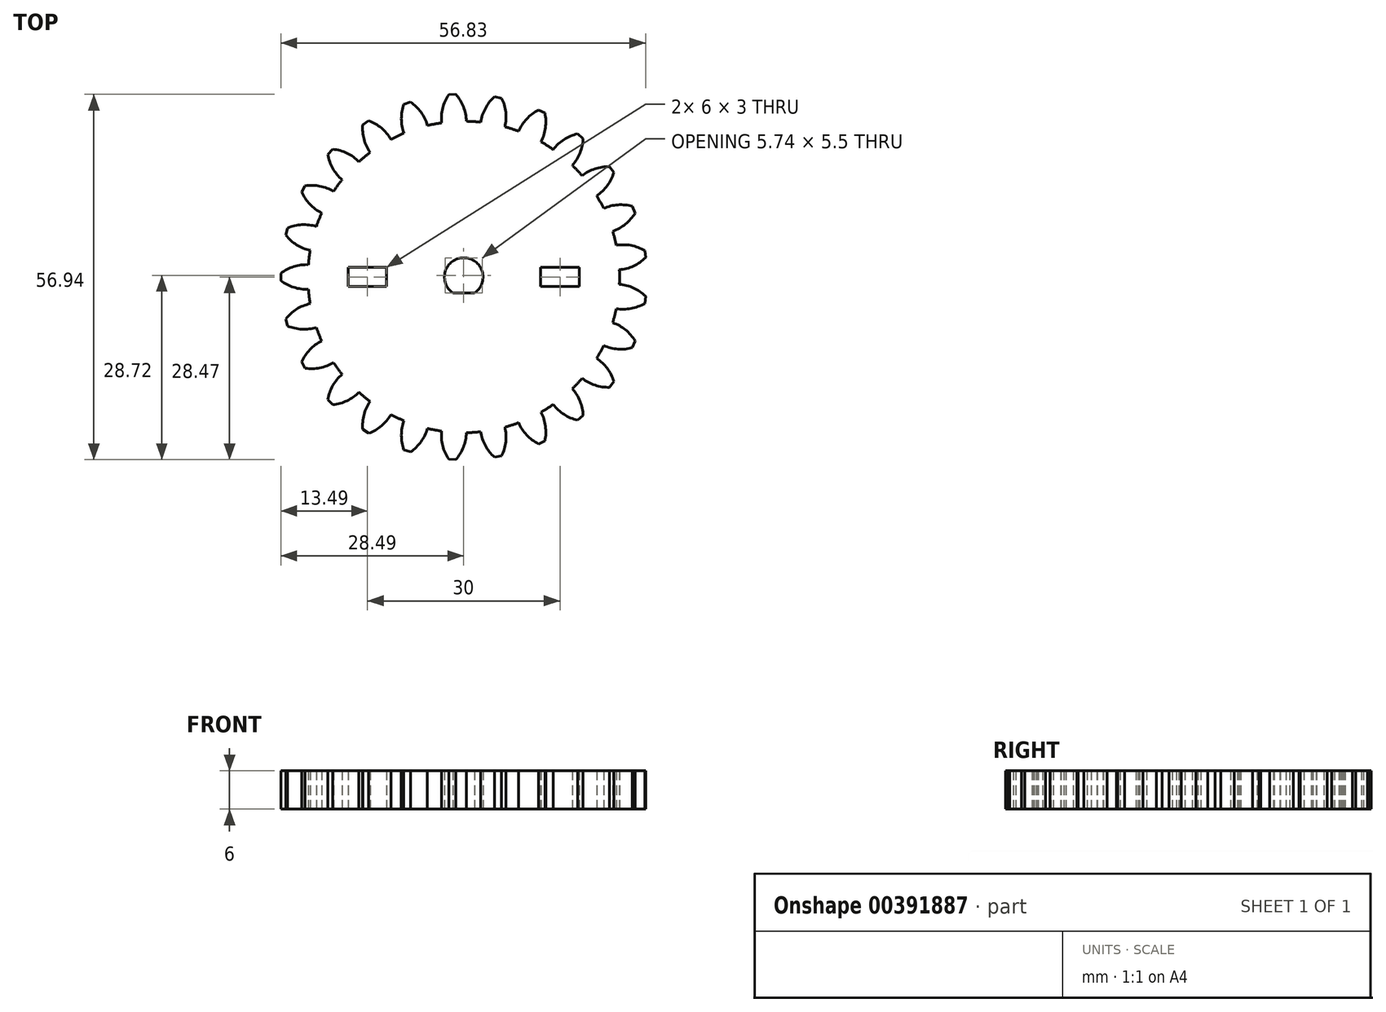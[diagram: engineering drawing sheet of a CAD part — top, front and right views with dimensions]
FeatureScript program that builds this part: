
annotation { "Feature Type Name" : "Feature", "Feature Type Description" : "" }
export const myFeature = defineFeature(function(context is Context, id is Id, definition is map)
    precondition{}
    {
        {
            assignVariable(context, id + "F0", {"name" : "GearDepth", "anyValue" : 6});
        }
        {
            var Q0;
            Q0=qCreatedBy(makeId("Top.planeOp"),FACE);
            var sketch = newSketch(context, id + "F1", { "sketchPlane" : qUnion([Q0])});
            skCircle(sketch, "E0", {"center": v(0, 0) * mm, "radius": 24.28 * mm, "construction": true});
            skCircle(sketch, "E1", {"center": v(0, 0) * mm, "radius": 26.39 * mm, "construction": true});
            skCircle(sketch, "E2", {"center": v(0, 0) * mm, "radius": 28.5 * mm, "construction": true});
            skLineSegment(sketch, "E3", {"start": v(0, 0) * mm, "end": v(0, 17.6) * mm, "construction": true});
            skLineSegment(sketch, "E4", {"start": v(0, 0) * mm, "end": v(-1.13, 18.01) * mm, "construction": true});
            skLineSegment(sketch, "E5", {"start": v(0, 26.39) * mm, "end": v(-10.54, 26.39) * mm, "construction": true});
            skLineSegment(sketch, "E6", {"start": v(0, 26.39) * mm, "end": v(-15.41, 20.78) * mm, "construction": true});
            skCircle(sketch, "E7", {"center": v(0, 26.39) * mm, "radius": 6.6 * mm, "construction": true});
            skCircle(sketch, "E8", {"center": v(-6.2, 24.13) * mm, "radius": 6.6 * mm, "construction": true});
            skArc(sketch, "E9.trimOffspring", {"start": v(0.4, 24.27) * mm, "mid": v(-0.05, 26.52) * mm, "end": v(-1.23, 28.47) * mm});
            skArc(sketch, "E10.MirrorCS", {"start": v(-3.44, 24.03) * mm, "mid": v(-3.28, 26.31) * mm, "end": v(-2.35, 28.4) * mm});
            skLineSegment(sketch, "E11", {"start": v(-2.35, 28.4) * mm, "end": v(-1.23, 28.47) * mm});
            skArc(sketch, "E12.1.0", {"start": v(-9.3, 22.42) * mm, "mid": v(-9.72, 24.67) * mm, "end": v(-9.34, 26.93) * mm});
            skArc(sketch, "E12.1.1", {"start": v(-5.65, 23.61) * mm, "mid": v(-6.64, 25.67) * mm, "end": v(-8.27, 27.27) * mm});
            skLineSegment(sketch, "E12.1.2", {"start": v(-9.34, 26.93) * mm, "end": v(-8.27, 27.27) * mm});
            skArc(sketch, "E12.2.0", {"start": v(-14.59, 19.4) * mm, "mid": v(-15.55, 21.48) * mm, "end": v(-15.74, 23.76) * mm});
            skArc(sketch, "E12.2.1", {"start": v(-11.35, 21.46) * mm, "mid": v(-12.82, 23.21) * mm, "end": v(-14.8, 24.36) * mm});
            skLineSegment(sketch, "E12.2.2", {"start": v(-15.74, 23.76) * mm, "end": v(-14.8, 24.36) * mm});
            skArc(sketch, "E12.3.0", {"start": v(-18.96, 15.17) * mm, "mid": v(-20.4, 16.94) * mm, "end": v(-21.15, 19.1) * mm});
            skArc(sketch, "E12.3.1", {"start": v(-16.33, 17.97) * mm, "mid": v(-18.19, 19.3) * mm, "end": v(-20.39, 19.91) * mm});
            skLineSegment(sketch, "E12.3.2", {"start": v(-21.15, 19.1) * mm, "end": v(-20.39, 19.91) * mm});
            skArc(sketch, "E12.4.0", {"start": v(-22.13, 9.98) * mm, "mid": v(-23.97, 11.33) * mm, "end": v(-25.24, 13.24) * mm});
            skArc(sketch, "E12.4.1", {"start": v(-20.28, 13.34) * mm, "mid": v(-22.42, 14.17) * mm, "end": v(-24.7, 14.22) * mm});
            skLineSegment(sketch, "E12.4.2", {"start": v(-25.24, 13.24) * mm, "end": v(-24.7, 14.22) * mm});
            skArc(sketch, "E12.5.0", {"start": v(-23.92, 4.16) * mm, "mid": v(-26.04, 5.02) * mm, "end": v(-27.74, 6.55) * mm});
            skArc(sketch, "E12.5.1", {"start": v(-22.96, 7.88) * mm, "mid": v(-25.23, 8.15) * mm, "end": v(-27.46, 7.63) * mm});
            skLineSegment(sketch, "E12.5.2", {"start": v(-27.74, 6.55) * mm, "end": v(-27.46, 7.63) * mm});
            skArc(sketch, "E12.6.0", {"start": v(-24.2, -1.92) * mm, "mid": v(-26.47, -1.62) * mm, "end": v(-28.5, -0.56) * mm});
            skArc(sketch, "E12.6.1", {"start": v(-24.2, 1.92) * mm, "mid": v(-26.47, 1.62) * mm, "end": v(-28.5, 0.56) * mm});
            skLineSegment(sketch, "E12.6.2", {"start": v(-28.5, -0.56) * mm, "end": v(-28.5, 0.56) * mm});
            skArc(sketch, "E12.7.0", {"start": v(-22.96, -7.88) * mm, "mid": v(-25.23, -8.15) * mm, "end": v(-27.46, -7.63) * mm});
            skArc(sketch, "E12.7.1", {"start": v(-23.92, -4.16) * mm, "mid": v(-26.04, -5.02) * mm, "end": v(-27.74, -6.55) * mm});
            skLineSegment(sketch, "E12.7.2", {"start": v(-27.46, -7.63) * mm, "end": v(-27.74, -6.55) * mm});
            skArc(sketch, "E12.8.0", {"start": v(-20.28, -13.34) * mm, "mid": v(-22.42, -14.17) * mm, "end": v(-24.7, -14.22) * mm});
            skArc(sketch, "E12.8.1", {"start": v(-22.13, -9.98) * mm, "mid": v(-23.97, -11.33) * mm, "end": v(-25.24, -13.24) * mm});
            skLineSegment(sketch, "E12.8.2", {"start": v(-24.7, -14.22) * mm, "end": v(-25.24, -13.24) * mm});
            skArc(sketch, "E12.9.0", {"start": v(-16.33, -17.97) * mm, "mid": v(-18.19, -19.3) * mm, "end": v(-20.39, -19.91) * mm});
            skArc(sketch, "E12.9.1", {"start": v(-18.96, -15.17) * mm, "mid": v(-20.4, -16.94) * mm, "end": v(-21.15, -19.1) * mm});
            skLineSegment(sketch, "E12.9.2", {"start": v(-20.39, -19.91) * mm, "end": v(-21.15, -19.1) * mm});
            skArc(sketch, "E13", {"start": v(-3.44, 24.03) * mm, "mid": v(-4.55, 23.85) * mm, "end": v(-5.65, 23.61) * mm});
            skArc(sketch, "E14.1.0", {"start": v(-9.3, 22.42) * mm, "mid": v(-10.34, 21.97) * mm, "end": v(-11.35, 21.46) * mm});
            skArc(sketch, "E14.2.0", {"start": v(-14.59, 19.4) * mm, "mid": v(-15.48, 18.7) * mm, "end": v(-16.33, 17.97) * mm});
            skArc(sketch, "E14.3.0", {"start": v(-18.96, 15.17) * mm, "mid": v(-19.64, 14.27) * mm, "end": v(-20.28, 13.34) * mm});
            skArc(sketch, "E14.4.0", {"start": v(-22.13, 9.98) * mm, "mid": v(-22.57, 8.94) * mm, "end": v(-22.96, 7.88) * mm});
            skArc(sketch, "E14.5.0", {"start": v(-23.92, 4.16) * mm, "mid": v(-24.09, 3.04) * mm, "end": v(-24.2, 1.92) * mm});
            skArc(sketch, "E14.6.0", {"start": v(-24.2, -1.92) * mm, "mid": v(-24.09, -3.04) * mm, "end": v(-23.92, -4.16) * mm});
            skArc(sketch, "E14.7.0", {"start": v(-22.96, -7.88) * mm, "mid": v(-22.57, -8.94) * mm, "end": v(-22.13, -9.98) * mm});
            skArc(sketch, "E14.8.0", {"start": v(-20.28, -13.34) * mm, "mid": v(-19.64, -14.27) * mm, "end": v(-18.96, -15.17) * mm});
            skArc(sketch, "E14.9.0", {"start": v(-16.33, -17.97) * mm, "mid": v(-15.48, -18.7) * mm, "end": v(-14.59, -19.4) * mm});
            skArc(sketch, "E15.3.10.0", {"start": v(-11.35, -21.46) * mm, "mid": v(-10.34, -21.97) * mm, "end": v(-9.3, -22.42) * mm});
            skArc(sketch, "E15.3.11.0", {"start": v(-5.65, -23.61) * mm, "mid": v(-4.55, -23.85) * mm, "end": v(-3.44, -24.03) * mm});
            skArc(sketch, "E15.3.12.0", {"start": v(0.4, -24.27) * mm, "mid": v(1.52, -24.23) * mm, "end": v(2.65, -24.13) * mm});
            skArc(sketch, "E15.3.13.0", {"start": v(6.42, -23.41) * mm, "mid": v(7.5, -23.09) * mm, "end": v(8.57, -22.72) * mm});
            skArc(sketch, "E15.3.14.0", {"start": v(12.04, -21.08) * mm, "mid": v(13, -20.5) * mm, "end": v(13.95, -19.87) * mm});
            skArc(sketch, "E16.4.10.0", {"start": v(-14.59, -19.4) * mm, "mid": v(-15.55, -21.48) * mm, "end": v(-15.74, -23.76) * mm});
            skArc(sketch, "E16.5.10.0", {"start": v(-11.35, -21.46) * mm, "mid": v(-12.82, -23.21) * mm, "end": v(-14.8, -24.36) * mm});
            skLineSegment(sketch, "E16.8.10.0", {"start": v(-14.8, -24.36) * mm, "end": v(-15.74, -23.76) * mm});
            skArc(sketch, "E16.4.11.0", {"start": v(-9.3, -22.42) * mm, "mid": v(-9.72, -24.67) * mm, "end": v(-9.34, -26.93) * mm});
            skArc(sketch, "E16.5.11.0", {"start": v(-5.65, -23.61) * mm, "mid": v(-6.64, -25.67) * mm, "end": v(-8.27, -27.27) * mm});
            skLineSegment(sketch, "E16.8.11.0", {"start": v(-8.27, -27.27) * mm, "end": v(-9.34, -26.93) * mm});
            skArc(sketch, "E16.4.12.0", {"start": v(-3.44, -24.03) * mm, "mid": v(-3.28, -26.31) * mm, "end": v(-2.35, -28.4) * mm});
            skArc(sketch, "E16.5.12.0", {"start": v(0.4, -24.27) * mm, "mid": v(-0.05, -26.52) * mm, "end": v(-1.23, -28.47) * mm});
            skLineSegment(sketch, "E16.8.12.0", {"start": v(-1.23, -28.47) * mm, "end": v(-2.35, -28.4) * mm});
            skArc(sketch, "E16.4.13.0", {"start": v(2.65, -24.13) * mm, "mid": v(3.37, -26.3) * mm, "end": v(4.8, -28.1) * mm});
            skArc(sketch, "E16.5.13.0", {"start": v(6.42, -23.41) * mm, "mid": v(6.55, -25.7) * mm, "end": v(5.89, -27.89) * mm});
            skLineSegment(sketch, "E16.8.13.0", {"start": v(5.89, -27.89) * mm, "end": v(4.8, -28.1) * mm});
            skArc(sketch, "E16.4.14.0", {"start": v(8.57, -22.72) * mm, "mid": v(9.8, -24.64) * mm, "end": v(11.63, -26.02) * mm});
            skArc(sketch, "E16.5.14.0", {"start": v(12.04, -21.08) * mm, "mid": v(12.73, -23.26) * mm, "end": v(12.64, -25.54) * mm});
            skLineSegment(sketch, "E16.8.14.0", {"start": v(12.64, -25.54) * mm, "end": v(11.63, -26.02) * mm});
            skArc(sketch, "E17.3.15.0", {"start": v(16.9, -17.42) * mm, "mid": v(17.7, -16.62) * mm, "end": v(18.45, -15.78) * mm});
            skArc(sketch, "E17.3.16.0", {"start": v(20.7, -12.67) * mm, "mid": v(21.27, -11.7) * mm, "end": v(21.8, -10.7) * mm});
            skArc(sketch, "E17.3.17.0", {"start": v(23.2, -7.12) * mm, "mid": v(23.52, -6.04) * mm, "end": v(23.77, -4.94) * mm});
            skArc(sketch, "E17.3.18.0", {"start": v(24.25, -1.13) * mm, "mid": v(24.28, 0) * mm, "end": v(24.25, 1.13) * mm});
            skArc(sketch, "E17.3.19.0", {"start": v(23.77, 4.94) * mm, "mid": v(23.52, 6.04) * mm, "end": v(23.2, 7.12) * mm});
            skArc(sketch, "E18.4.15.0", {"start": v(13.95, -19.87) * mm, "mid": v(15.63, -21.42) * mm, "end": v(17.73, -22.31) * mm});
            skArc(sketch, "E18.5.15.0", {"start": v(16.9, -17.42) * mm, "mid": v(18.12, -19.36) * mm, "end": v(18.6, -21.6) * mm});
            skLineSegment(sketch, "E18.8.15.0", {"start": v(18.6, -21.6) * mm, "end": v(17.73, -22.31) * mm});
            skArc(sketch, "E18.4.16.0", {"start": v(18.45, -15.78) * mm, "mid": v(20.46, -16.87) * mm, "end": v(22.72, -17.2) * mm});
            skArc(sketch, "E18.5.16.0", {"start": v(20.7, -12.67) * mm, "mid": v(22.36, -14.25) * mm, "end": v(23.38, -16.3) * mm});
            skLineSegment(sketch, "E18.8.16.0", {"start": v(23.38, -16.3) * mm, "end": v(22.72, -17.2) * mm});
            skArc(sketch, "E18.4.17.0", {"start": v(21.8, -10.7) * mm, "mid": v(24.01, -11.25) * mm, "end": v(26.29, -11) * mm});
            skArc(sketch, "E18.5.17.0", {"start": v(23.2, -7.12) * mm, "mid": v(25.2, -8.24) * mm, "end": v(26.7, -9.97) * mm});
            skLineSegment(sketch, "E18.8.17.0", {"start": v(26.7, -9.97) * mm, "end": v(26.29, -11) * mm});
            skArc(sketch, "E18.4.18.0", {"start": v(23.77, -4.94) * mm, "mid": v(26.06, -4.92) * mm, "end": v(28.2, -4.13) * mm});
            skArc(sketch, "E18.5.18.0", {"start": v(24.25, -1.13) * mm, "mid": v(26.46, -1.71) * mm, "end": v(28.34, -3.02) * mm});
            skLineSegment(sketch, "E18.8.18.0", {"start": v(28.34, -3.02) * mm, "end": v(28.2, -4.13) * mm});
            skArc(sketch, "E18.4.19.0", {"start": v(24.25, 1.13) * mm, "mid": v(26.46, 1.71) * mm, "end": v(28.34, 3.02) * mm});
            skArc(sketch, "E18.5.19.0", {"start": v(23.77, 4.94) * mm, "mid": v(26.06, 4.92) * mm, "end": v(28.2, 4.13) * mm});
            skLineSegment(sketch, "E18.8.19.0", {"start": v(28.2, 4.13) * mm, "end": v(28.34, 3.02) * mm});
            skCircle(sketch, "E19", {"center": v(0, 0) * mm, "radius": 2.5 * mm, "construction": true});
            skArc(sketch, "E20.3.20.0", {"start": v(21.8, 10.7) * mm, "mid": v(21.27, 11.7) * mm, "end": v(20.7, 12.67) * mm});
            skArc(sketch, "E20.3.21.0", {"start": v(18.45, 15.78) * mm, "mid": v(17.7, 16.62) * mm, "end": v(16.9, 17.42) * mm});
            skArc(sketch, "E20.3.22.0", {"start": v(13.95, 19.87) * mm, "mid": v(13, 20.5) * mm, "end": v(12.04, 21.08) * mm});
            skArc(sketch, "E20.3.23.0", {"start": v(8.57, 22.72) * mm, "mid": v(7.5, 23.09) * mm, "end": v(6.42, 23.41) * mm});
            skArc(sketch, "E20.3.24.0", {"start": v(2.65, 24.13) * mm, "mid": v(1.52, 24.23) * mm, "end": v(0.4, 24.27) * mm});
            skArc(sketch, "E21.4.20.0", {"start": v(23.2, 7.12) * mm, "mid": v(25.2, 8.24) * mm, "end": v(26.7, 9.97) * mm});
            skArc(sketch, "E21.5.20.0", {"start": v(21.8, 10.7) * mm, "mid": v(24.01, 11.25) * mm, "end": v(26.29, 11) * mm});
            skLineSegment(sketch, "E21.8.20.0", {"start": v(26.29, 11) * mm, "end": v(26.7, 9.97) * mm});
            skArc(sketch, "E21.4.21.0", {"start": v(20.7, 12.67) * mm, "mid": v(22.36, 14.25) * mm, "end": v(23.38, 16.3) * mm});
            skArc(sketch, "E21.5.21.0", {"start": v(18.45, 15.78) * mm, "mid": v(20.46, 16.87) * mm, "end": v(22.72, 17.2) * mm});
            skLineSegment(sketch, "E21.8.21.0", {"start": v(22.72, 17.2) * mm, "end": v(23.38, 16.3) * mm});
            skArc(sketch, "E21.4.22.0", {"start": v(16.9, 17.42) * mm, "mid": v(18.12, 19.36) * mm, "end": v(18.6, 21.6) * mm});
            skArc(sketch, "E21.5.22.0", {"start": v(13.95, 19.87) * mm, "mid": v(15.63, 21.42) * mm, "end": v(17.73, 22.31) * mm});
            skLineSegment(sketch, "E21.8.22.0", {"start": v(17.73, 22.31) * mm, "end": v(18.6, 21.6) * mm});
            skArc(sketch, "E21.4.23.0", {"start": v(12.04, 21.08) * mm, "mid": v(12.73, 23.26) * mm, "end": v(12.64, 25.54) * mm});
            skArc(sketch, "E21.5.23.0", {"start": v(8.57, 22.72) * mm, "mid": v(9.8, 24.64) * mm, "end": v(11.63, 26.02) * mm});
            skLineSegment(sketch, "E21.8.23.0", {"start": v(11.63, 26.02) * mm, "end": v(12.64, 25.54) * mm});
            skArc(sketch, "E21.4.24.0", {"start": v(6.42, 23.41) * mm, "mid": v(6.55, 25.7) * mm, "end": v(5.89, 27.89) * mm});
            skArc(sketch, "E21.5.24.0", {"start": v(2.65, 24.13) * mm, "mid": v(3.37, 26.3) * mm, "end": v(4.8, 28.1) * mm});
            skLineSegment(sketch, "E21.8.24.0", {"start": v(4.8, 28.1) * mm, "end": v(5.89, 27.89) * mm});
            skLineSegment(sketch, "E22", {"start": v(-1.66, -2.5) * mm, "end": v(1.66, -2.5) * mm});
            skArc(sketch, "E23", {"start": v(-1.66, -2.5) * mm, "mid": v(0, 3) * mm, "end": v(1.66, -2.5) * mm});
            skLineSegment(sketch, "E24.bottom", {"start": v(18, -1.5) * mm, "end": v(12, -1.5) * mm});
            skLineSegment(sketch, "E24.top", {"start": v(18, 1.5) * mm, "end": v(12, 1.5) * mm});
            skLineSegment(sketch, "E24.left", {"start": v(18, -1.5) * mm, "end": v(18, 1.5) * mm});
            skLineSegment(sketch, "E24.right", {"start": v(12, -1.5) * mm, "end": v(12, 1.5) * mm});
            skPoint(sketch, "E24.middle", {"position": v(15, 0) * mm});
            skLineSegment(sketch, "E25.bottom", {"start": v(-12, -1.5) * mm, "end": v(-18, -1.5) * mm});
            skLineSegment(sketch, "E25.top", {"start": v(-12, 1.5) * mm, "end": v(-18, 1.5) * mm});
            skLineSegment(sketch, "E25.left", {"start": v(-12, -1.5) * mm, "end": v(-12, 1.5) * mm});
            skLineSegment(sketch, "E25.right", {"start": v(-18, -1.5) * mm, "end": v(-18, 1.5) * mm});
            skPoint(sketch, "E25.middle", {"position": v(-15, 0) * mm});
            skSolve(sketch);
        }
        {
            var Q0;
            {var subQ0=sQuery(id+"F1.wireOp",EDGE,"E9.trimOffspring");Q0=makeQuery(id+"F1.imprint","IMPRINT",FACE,{"disambiguationData":[TD([[makeQuery(id+"F1.imprint","IMPRINT",EDGE,{"derivedFrom":subQ0}),1.0]])]});}
            var Q1;
            {var subQ0=sQuery(id+"F1.wireOp",EDGE,"E0");var subQ1=makeQuery(id+"F1.imprint","INTERSECT",VERTEX,{"derivedFrom":[subQ0,sQuery(id+"F1.wireOp",EDGE,"E9.trimOffspring")]});Q1=makeQuery(id+"F1.imprint","IMPRINT",FACE,{"disambiguationData":[TD([[makeQuery(id+"F1.imprint","IMPRINT",EDGE,{"disambiguationData":[TD([[subQ1,-1.0]])],"derivedFrom":subQ0}),1.0]])]});}
            var Q2;
            {var subQ0=sQuery(id+"F1.wireOp",EDGE,"ff0f1e59-5a19-46eb-ac47-c6f22bc8a670.1.0");Q2=makeQuery(id+"F1.imprint","IMPRINT",FACE,{"disambiguationData":[TD([[makeQuery(id+"F1.imprint","IMPRINT",EDGE,{"derivedFrom":subQ0}),1.0]])]});}
            var Q3;
            {var subQ0=sQuery(id+"F1.wireOp",EDGE,"ff0f1e59-5a19-46eb-ac47-c6f22bc8a670.2.0");Q3=makeQuery(id+"F1.imprint","IMPRINT",FACE,{"disambiguationData":[TD([[makeQuery(id+"F1.imprint","IMPRINT",EDGE,{"derivedFrom":subQ0}),1.0]])]});}
            var Q4;
            {var subQ0=sQuery(id+"F1.wireOp",EDGE,"ff0f1e59-5a19-46eb-ac47-c6f22bc8a670.3.0");Q4=makeQuery(id+"F1.imprint","IMPRINT",FACE,{"disambiguationData":[TD([[makeQuery(id+"F1.imprint","IMPRINT",EDGE,{"derivedFrom":subQ0}),1.0]])]});}
            var Q5;
            {var subQ0=sQuery(id+"F1.wireOp",EDGE,"ff0f1e59-5a19-46eb-ac47-c6f22bc8a670.4.0");Q5=makeQuery(id+"F1.imprint","IMPRINT",FACE,{"disambiguationData":[TD([[makeQuery(id+"F1.imprint","IMPRINT",EDGE,{"derivedFrom":subQ0}),1.0]])]});}
            var Q6;
            {var subQ0=sQuery(id+"F1.wireOp",EDGE,"ff0f1e59-5a19-46eb-ac47-c6f22bc8a670.5.0");Q6=makeQuery(id+"F1.imprint","IMPRINT",FACE,{"disambiguationData":[TD([[makeQuery(id+"F1.imprint","IMPRINT",EDGE,{"derivedFrom":subQ0}),1.0]])]});}
            var Q7;
            {var subQ0=sQuery(id+"F1.wireOp",EDGE,"ff0f1e59-5a19-46eb-ac47-c6f22bc8a670.6.0");Q7=makeQuery(id+"F1.imprint","IMPRINT",FACE,{"disambiguationData":[TD([[makeQuery(id+"F1.imprint","IMPRINT",EDGE,{"derivedFrom":subQ0}),1.0]])]});}
            var Q8;
            {var subQ0=sQuery(id+"F1.wireOp",EDGE,"ff0f1e59-5a19-46eb-ac47-c6f22bc8a670.7.0");Q8=makeQuery(id+"F1.imprint","IMPRINT",FACE,{"disambiguationData":[TD([[makeQuery(id+"F1.imprint","IMPRINT",EDGE,{"derivedFrom":subQ0}),1.0]])]});}
            var Q9;
            {var subQ0=sQuery(id+"F1.wireOp",EDGE,"ff0f1e59-5a19-46eb-ac47-c6f22bc8a670.8.0");Q9=makeQuery(id+"F1.imprint","IMPRINT",FACE,{"disambiguationData":[TD([[makeQuery(id+"F1.imprint","IMPRINT",EDGE,{"derivedFrom":subQ0}),1.0]])]});}
            var Q10;
            {var subQ0=sQuery(id+"F1.wireOp",EDGE,"ff0f1e59-5a19-46eb-ac47-c6f22bc8a670.9.0");Q10=makeQuery(id+"F1.imprint","IMPRINT",FACE,{"disambiguationData":[TD([[makeQuery(id+"F1.imprint","IMPRINT",EDGE,{"derivedFrom":subQ0}),1.0]])]});}
            var Q11;
            {var subQ0=sQuery(id+"F1.wireOp",EDGE,"ff0f1e59-5a19-46eb-ac47-c6f22bc8a670.10.0");Q11=makeQuery(id+"F1.imprint","IMPRINT",FACE,{"disambiguationData":[TD([[makeQuery(id+"F1.imprint","IMPRINT",EDGE,{"derivedFrom":subQ0}),1.0]])]});}
            var Q12;
            {var subQ0=sQuery(id+"F1.wireOp",EDGE,"ff0f1e59-5a19-46eb-ac47-c6f22bc8a670.11.0");Q12=makeQuery(id+"F1.imprint","IMPRINT",FACE,{"disambiguationData":[TD([[makeQuery(id+"F1.imprint","IMPRINT",EDGE,{"derivedFrom":subQ0}),1.0]])]});}
            var Q13;
            {var subQ0=sQuery(id+"F1.wireOp",EDGE,"ff0f1e59-5a19-46eb-ac47-c6f22bc8a670.12.0");Q13=makeQuery(id+"F1.imprint","IMPRINT",FACE,{"disambiguationData":[TD([[makeQuery(id+"F1.imprint","IMPRINT",EDGE,{"derivedFrom":subQ0}),1.0]])]});}
            var Q14;
            {var subQ0=sQuery(id+"F1.wireOp",EDGE,"ff0f1e59-5a19-46eb-ac47-c6f22bc8a670.13.0");Q14=makeQuery(id+"F1.imprint","IMPRINT",FACE,{"disambiguationData":[TD([[makeQuery(id+"F1.imprint","IMPRINT",EDGE,{"derivedFrom":subQ0}),1.0]])]});}
            var Q15;
            {var subQ0=sQuery(id+"F1.wireOp",EDGE,"ff0f1e59-5a19-46eb-ac47-c6f22bc8a670.14.0");Q15=makeQuery(id+"F1.imprint","IMPRINT",FACE,{"disambiguationData":[TD([[makeQuery(id+"F1.imprint","IMPRINT",EDGE,{"derivedFrom":subQ0}),1.0]])]});}
            var Q16;
            {var subQ0=sQuery(id+"F1.wireOp",EDGE,"ff0f1e59-5a19-46eb-ac47-c6f22bc8a670.15.0");Q16=makeQuery(id+"F1.imprint","IMPRINT",FACE,{"disambiguationData":[TD([[makeQuery(id+"F1.imprint","IMPRINT",EDGE,{"derivedFrom":subQ0}),1.0]])]});}
            var Q17;
            {var subQ0=sQuery(id+"F1.wireOp",EDGE,"ff0f1e59-5a19-46eb-ac47-c6f22bc8a670.16.0");Q17=makeQuery(id+"F1.imprint","IMPRINT",FACE,{"disambiguationData":[TD([[makeQuery(id+"F1.imprint","IMPRINT",EDGE,{"derivedFrom":subQ0}),1.0]])]});}
            var Q18;
            {var subQ0=sQuery(id+"F1.wireOp",EDGE,"ff0f1e59-5a19-46eb-ac47-c6f22bc8a670.17.0");Q18=makeQuery(id+"F1.imprint","IMPRINT",FACE,{"disambiguationData":[TD([[makeQuery(id+"F1.imprint","IMPRINT",EDGE,{"derivedFrom":subQ0}),1.0]])]});}
            var Q19;
            {var subQ0=sQuery(id+"F1.wireOp",EDGE,"ff0f1e59-5a19-46eb-ac47-c6f22bc8a670.18.0");Q19=makeQuery(id+"F1.imprint","IMPRINT",FACE,{"disambiguationData":[TD([[makeQuery(id+"F1.imprint","IMPRINT",EDGE,{"derivedFrom":subQ0}),1.0]])]});}
            var Q20;
            {var subQ0=sQuery(id+"F1.wireOp",EDGE,"ff0f1e59-5a19-46eb-ac47-c6f22bc8a670.19.0");Q20=makeQuery(id+"F1.imprint","IMPRINT",FACE,{"disambiguationData":[TD([[makeQuery(id+"F1.imprint","IMPRINT",EDGE,{"derivedFrom":subQ0}),1.0]])]});}
            var Q21;
            Q21=sQuery(id+"F1.wireOp",EDGE,"E0");
            var Q22;
            Q22=sQuery(id+"F1.wireOp",EDGE,"E9.trimOffspring");
            var Q23;
            Q23=sQuery(id+"F1.wireOp",EDGE,"E11");
            var Q24;
            Q24=sQuery(id+"F1.wireOp",EDGE,"E10.MirrorCS");
            extrude(context, id + "F2", {"entities" : qUnion([Q0, Q1, Q2, Q3, Q4, Q5, Q6, Q7, Q8, Q9, Q10, Q11, Q12, Q13, Q14, Q15, Q16, Q17, Q18, Q19, Q20]), "surfaceEntities" : qUnion([Q21, Q22, Q23, Q24]), "depth" : (getVariable(context, 'GearDepth')) * mm});
        }
    });
